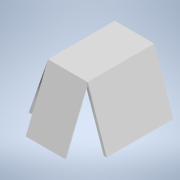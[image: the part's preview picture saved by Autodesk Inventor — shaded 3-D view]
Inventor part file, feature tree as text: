
AUTODESK INVENTOR PART (.ipt)
format: ipt  version: 2021 (Build 250183000, 183)  size: 119,296 bytes
history: native  units: mm
features: extrude x3, sketch x3, other x1, plane x1
ambient origin geometry x8: Origin, YZ Plane, XZ Plane, XY Plane, X Axis, Y Axis, Z Axis, Center Point
bodies: Body1 (feature_tree)
feature tree (8):
  other  "Sólido1"
  extrude  "Extrusión1"  Depth=200.0mm
  extrude  "Extrusión2"  Depth=10.0mm
  plane  "Plano de trabajo2"
  extrude  "Extrusión3"  Depth=10.0mm
  sketch  "Boceto1"  dims[d0=280.0mm d1=200.0mm]
  sketch  "Boceto2"  dims[d2=240.0mm d3=0.0mm d4=10.0mm]
  sketch  "Boceto4"  dims[d7=10.0mm d8=10.0mm d9=240.0mm d10=0.0mm d11=80.0mm d12=141.908mm d13=0.0mm d14=200.0mm]
